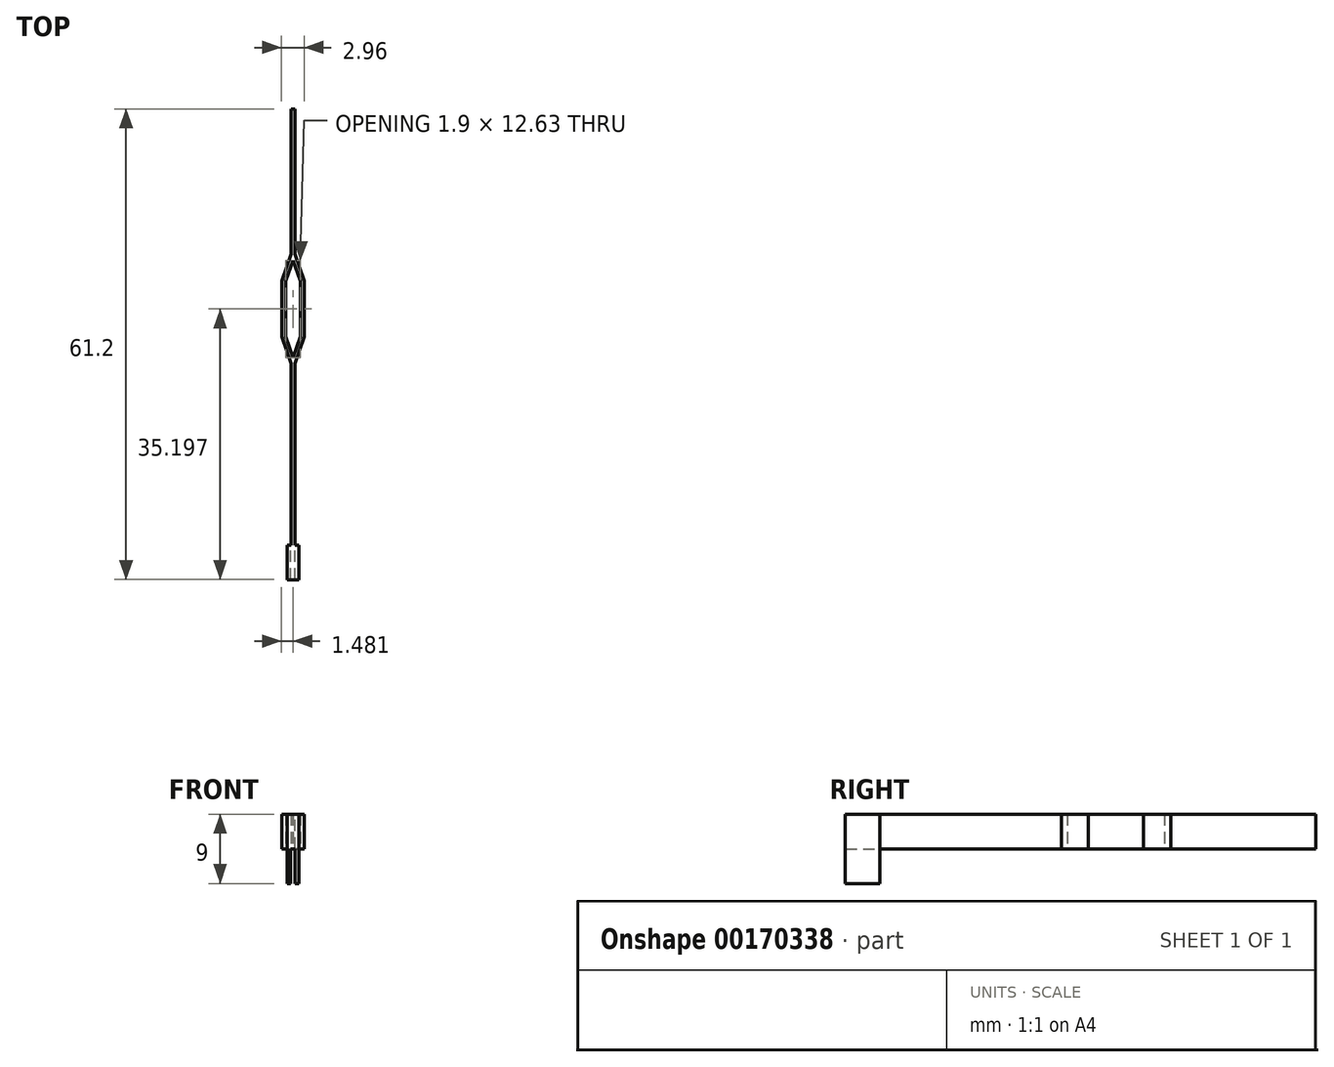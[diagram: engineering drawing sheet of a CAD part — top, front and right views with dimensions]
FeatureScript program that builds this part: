
annotation { "Feature Type Name" : "Feature", "Feature Type Description" : "" }
export const myFeature = defineFeature(function(context is Context, id is Id, definition is map)
    precondition{}
    {
        {
            var Q0;
            Q0=qCreatedBy(makeId("Top.planeOp"),FACE);
            var sketch = newSketch(context, id + "F0", { "sketchPlane" : qUnion([Q0])});
            skLineSegment(sketch, "E0.bottom", {"start": v(-0.97, 27.7) * mm, "end": v(-0.47, 27.7) * mm});
            skLineSegment(sketch, "E0.top", {"start": v(-0.97, -33.5) * mm, "end": v(-0.47, -33.5) * mm});
            skLineSegment(sketch, "E1.bottom", {"start": v(-1.67, 5.3) * mm, "end": v(0.23, 5.3) * mm});
            skLineSegment(sketch, "E1.top", {"start": v(-1.67, -1.9) * mm, "end": v(0.23, -1.9) * mm});
            skLineSegment(sketch, "E1.left", {"start": v(-1.67, 5.3) * mm, "end": v(-1.67, -1.9) * mm});
            skLineSegment(sketch, "E1.right", {"start": v(0.23, 5.3) * mm, "end": v(0.23, -1.9) * mm});
            skLineSegment(sketch, "E2", {"start": v(-1.67, 5.3) * mm, "end": v(-0.97, 7.3) * mm});
            skLineSegment(sketch, "E3", {"start": v(-0.47, 7.3) * mm, "end": v(0.23, 5.3) * mm});
            skLineSegment(sketch, "E4", {"start": v(-1.67, -1.9) * mm, "end": v(-0.97, -3.9) * mm});
            skLineSegment(sketch, "E5", {"start": v(-0.47, -3.9) * mm, "end": v(0.23, -1.9) * mm});
            skLineSegment(sketch, "E6", {"start": v(-0.97, 8.82) * mm, "end": v(-2.2, 5.3) * mm});
            skLineSegment(sketch, "E7", {"start": v(-2.2, 5.3) * mm, "end": v(-2.2, -1.9) * mm});
            skLineSegment(sketch, "E8", {"start": v(-2.2, -1.9) * mm, "end": v(-0.97, -5.4) * mm});
            skLineSegment(sketch, "E9", {"start": v(-0.47, 8.82) * mm, "end": v(0.76, 5.3) * mm});
            skLineSegment(sketch, "E10", {"start": v(0.76, 5.3) * mm, "end": v(0.76, -1.9) * mm});
            skLineSegment(sketch, "E11", {"start": v(0.76, -1.9) * mm, "end": v(-0.47, -5.4) * mm});
            skLineSegment(sketch, "E12", {"start": v(-0.97, 27.7) * mm, "end": v(-0.97, 8.82) * mm});
            skLineSegment(sketch, "E13", {"start": v(-0.97, -5.4) * mm, "end": v(-0.97, -33.5) * mm});
            skLineSegment(sketch, "E14", {"start": v(-0.47, 27.7) * mm, "end": v(-0.47, 8.82) * mm});
            skLineSegment(sketch, "E15", {"start": v(-0.47, -5.4) * mm, "end": v(-0.47, -33.5) * mm});
            skLineSegment(sketch, "E16", {"start": v(-0.47, 7.3) * mm, "end": v(-0.72, 8.02) * mm});
            skLineSegment(sketch, "E17", {"start": v(-0.72, 8.02) * mm, "end": v(-0.97, 7.3) * mm});
            skLineSegment(sketch, "E18", {"start": v(-0.47, -3.9) * mm, "end": v(-0.72, -4.6) * mm});
            skLineSegment(sketch, "E19", {"start": v(-0.97, -3.9) * mm, "end": v(-0.72, -4.6) * mm});
            skSolve(sketch);
        }
        {
            var Q0;
            Q0=makeQuery(id+"F0.imprint","IMPRINT",FACE,{"disambiguationData":[TD([[makeQuery(id+"F0.imprint","IMPRINT",EDGE,{"derivedFrom":sQuery(id+"F0.wireOp",EDGE,"E0.bottom")}),-1.0]])]});
            var Q1;
            Q1=sQuery(id+"F0.wireOp",EDGE,"E3");
            var Q2;
            Q2=sQuery(id+"F0.wireOp",EDGE,"E1.right");
            var Q3;
            Q3=sQuery(id+"F0.wireOp",EDGE,"E5");
            var Q4;
            Q4=sQuery(id+"F0.wireOp",EDGE,"nkD4Ib0B-5Y8a-obz0-IcfC-dqy6glZyB51n");
            var Q5;
            Q5=sQuery(id+"F0.wireOp",EDGE,"diSldYqd-0EJK-Tftk-uqzO-esxdoyUf5riP");
            var Q6;
            Q6=sQuery(id+"F0.wireOp",EDGE,"E1.left");
            var Q7;
            Q7=sQuery(id+"F0.wireOp",EDGE,"E2");
            var Q8;
            Q8=sQuery(id+"F0.wireOp",EDGE,"E4");
            var Q9;
            Q9=sQuery(id+"F0.wireOp",EDGE,"E8");
            var Q10;
            Q10=sQuery(id+"F0.wireOp",EDGE,"E7");
            var Q11;
            Q11=sQuery(id+"F0.wireOp",EDGE,"E10");
            var Q12;
            Q12=sQuery(id+"F0.wireOp",EDGE,"E11");
            var Q13;
            Q13=sQuery(id+"F0.wireOp",EDGE,"E14");
            var Q14;
            Q14=sQuery(id+"F0.wireOp",EDGE,"E12");
            var Q15;
            Q15=sQuery(id+"F0.wireOp",EDGE,"E6");
            var Q16;
            Q16=sQuery(id+"F0.wireOp",EDGE,"E9");
            var Q17;
            Q17=sQuery(id+"F0.wireOp",EDGE,"E0.bottom");
            var Q18;
            Q18=sQuery(id+"F0.wireOp",EDGE,"E15");
            var Q19;
            Q19=sQuery(id+"F0.wireOp",EDGE,"E13");
            var Q20;
            Q20=sQuery(id+"F0.wireOp",EDGE,"E0.top");
            extrude(context, id + "F1", {"entities" : qUnion([Q0]), "surfaceEntities" : qUnion([Q1, Q2, Q3, Q4, Q5, Q6, Q7, Q8, Q9, Q10, Q11, Q12, Q13, Q14, Q15, Q16, Q17, Q18, Q19, Q20]), "depth" : 4.5 * mm});
        }
        {
            var Q0;
            Q0=makeQuery(id+"F1.opExtrude","CAP_FACE",FACE,{"disambiguationData":[OSD([sQuery(id+"F0.wireOp",EDGE,"E0.bottom"),sQuery(id+"F0.wireOp",EDGE,"E0.top"),sQuery(id+"F0.wireOp",EDGE,"E1.left"),sQuery(id+"F0.wireOp",EDGE,"E1.right"),sQuery(id+"F0.wireOp",EDGE,"E2"),sQuery(id+"F0.wireOp",EDGE,"E3"),sQuery(id+"F0.wireOp",EDGE,"E4"),sQuery(id+"F0.wireOp",EDGE,"E5"),sQuery(id+"F0.wireOp",EDGE,"E6"),sQuery(id+"F0.wireOp",EDGE,"E7"),sQuery(id+"F0.wireOp",EDGE,"E8"),sQuery(id+"F0.wireOp",EDGE,"E9"),sQuery(id+"F0.wireOp",EDGE,"E10"),sQuery(id+"F0.wireOp",EDGE,"E11"),sQuery(id+"F0.wireOp",EDGE,"E12"),sQuery(id+"F0.wireOp",EDGE,"E13"),sQuery(id+"F0.wireOp",EDGE,"E14"),sQuery(id+"F0.wireOp",EDGE,"E15"),sQuery(id+"F0.wireOp",EDGE,"E16"),sQuery(id+"F0.wireOp",EDGE,"E17"),sQuery(id+"F0.wireOp",EDGE,"E18"),sQuery(id+"F0.wireOp",EDGE,"E19")])],"isStart":false});
            var sketch = newSketch(context, id + "F2", { "sketchPlane" : qUnion([Q0])});
            skLineSegment(sketch, "E20.bottom", {"start": v(-0.47, -33.5) * mm, "end": v(0.03, -33.5) * mm});
            skLineSegment(sketch, "E20.top", {"start": v(-0.47, -29) * mm, "end": v(0.03, -29) * mm});
            skLineSegment(sketch, "E20.left", {"start": v(-0.47, -33.5) * mm, "end": v(-0.47, -29) * mm});
            skLineSegment(sketch, "E20.right", {"start": v(0.03, -33.5) * mm, "end": v(0.03, -29) * mm});
            skLineSegment(sketch, "E21.bottom", {"start": v(-0.97, -33.5) * mm, "end": v(-1.47, -33.5) * mm});
            skLineSegment(sketch, "E21.top", {"start": v(-0.97, -29) * mm, "end": v(-1.47, -29) * mm});
            skLineSegment(sketch, "E21.left", {"start": v(-0.97, -33.5) * mm, "end": v(-0.97, -29) * mm});
            skLineSegment(sketch, "E21.right", {"start": v(-1.47, -33.5) * mm, "end": v(-1.47, -29) * mm});
            skSolve(sketch);
        }
        {
            var Q0;
            Q0=makeQuery(id+"F2.imprint","IMPRINT",FACE,{"disambiguationData":[TD([[makeQuery(id+"F2.imprint","IMPRINT",EDGE,{"derivedFrom":sQuery(id+"F2.wireOp",EDGE,"E21.bottom")}),-1.0]])]});
            var Q1;
            Q1=makeQuery(id+"F2.imprint","IMPRINT",FACE,{"disambiguationData":[TD([[makeQuery(id+"F2.imprint","IMPRINT",EDGE,{"derivedFrom":sQuery(id+"F2.wireOp",EDGE,"E20.bottom")}),1.0]])]});
            extrude(context, id + "F3", {"entities" : qUnion([Q0, Q1]), "operationType" : NewBodyOperationType.ADD, "oppositeDirection" : true, "depth" : 9 * mm});
        }
        {
            var Q0;
            Q0=makeQuery(id+"F1.opExtrude","CAP_FACE",FACE,{"disambiguationData":[OSD([sQuery(id+"F0.wireOp",EDGE,"E0.bottom"),sQuery(id+"F0.wireOp",EDGE,"E0.top"),sQuery(id+"F0.wireOp",EDGE,"E1.left"),sQuery(id+"F0.wireOp",EDGE,"E1.right"),sQuery(id+"F0.wireOp",EDGE,"E2"),sQuery(id+"F0.wireOp",EDGE,"E3"),sQuery(id+"F0.wireOp",EDGE,"E4"),sQuery(id+"F0.wireOp",EDGE,"E5"),sQuery(id+"F0.wireOp",EDGE,"E6"),sQuery(id+"F0.wireOp",EDGE,"E7"),sQuery(id+"F0.wireOp",EDGE,"E8"),sQuery(id+"F0.wireOp",EDGE,"E9"),sQuery(id+"F0.wireOp",EDGE,"E10"),sQuery(id+"F0.wireOp",EDGE,"E11"),sQuery(id+"F0.wireOp",EDGE,"E12"),sQuery(id+"F0.wireOp",EDGE,"E13"),sQuery(id+"F0.wireOp",EDGE,"E14"),sQuery(id+"F0.wireOp",EDGE,"E15"),sQuery(id+"F0.wireOp",EDGE,"E16"),sQuery(id+"F0.wireOp",EDGE,"E17"),sQuery(id+"F0.wireOp",EDGE,"E18"),sQuery(id+"F0.wireOp",EDGE,"E19")])],"isStart":true});
            var sketch = newSketch(context, id + "F4", { "sketchPlane" : qUnion([Q0])});
            skLineSegment(sketch, "E22.bottom", {"start": v(-1.02, 33.5) * mm, "end": v(-0.42, 33.5) * mm});
            skLineSegment(sketch, "E22.top", {"start": v(-1.02, 29) * mm, "end": v(-0.42, 29) * mm});
            skLineSegment(sketch, "E22.left", {"start": v(-1.02, 33.5) * mm, "end": v(-1.02, 29) * mm});
            skLineSegment(sketch, "E22.right", {"start": v(-0.42, 33.5) * mm, "end": v(-0.42, 29) * mm});
            skSolve(sketch);
        }
        {
            var Q0;
            {var subQ10=sQuery(id+"F4.wireOp",EDGE,"E22.left");Q0=makeQuery(id+"F4.imprint","IMPRINT",FACE,{"disambiguationData":[TD([[makeQuery(id+"F4.imprint","IMPRINT",EDGE,{"derivedFrom":subQ10}),1.0]])]});}
            var Q1;
            {var subQ10=sQuery(id+"F4.wireOp",EDGE,"E22.right");Q1=makeQuery(id+"F4.imprint","IMPRINT",FACE,{"disambiguationData":[TD([[makeQuery(id+"F4.imprint","IMPRINT",EDGE,{"derivedFrom":subQ10}),-1.0]])]});}
            extrude(context, id + "F5", {"entities" : qUnion([Q0, Q1]), "operationType" : NewBodyOperationType.REMOVE, "depth" : 25 * mm});
        }
    });
